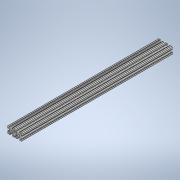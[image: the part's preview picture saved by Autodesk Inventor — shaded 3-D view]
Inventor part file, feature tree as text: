
AUTODESK INVENTOR PART (.ipt)
format: ipt  version: 2020 (Build 240168000, 168)  size: 333,824 bytes
history: native  units: in
note: dims shown in document units (in); Inventor stores cm internally (conversion verified against a paired STEP export)
features: sketch x2, extrude x1
ambient origin geometry x8: Origin, YZ Plane, XZ Plane, XY Plane, X Axis, Y Axis, Z Axis, Center Point
bodies: Solid1 (feature_tree)
feature tree (3):
  extrude  "Extrusion1"  [1 undecoded]
  sketch  "Sketch2"
  sketch  "Sketch1"  dims[d0=21.0in d1=0.0in]
note: 1 required parameter value undecoded (feature->parameter linkage not recoverable at this tier; creation-order binding heuristic only, values carry confidence <= 0.55)
